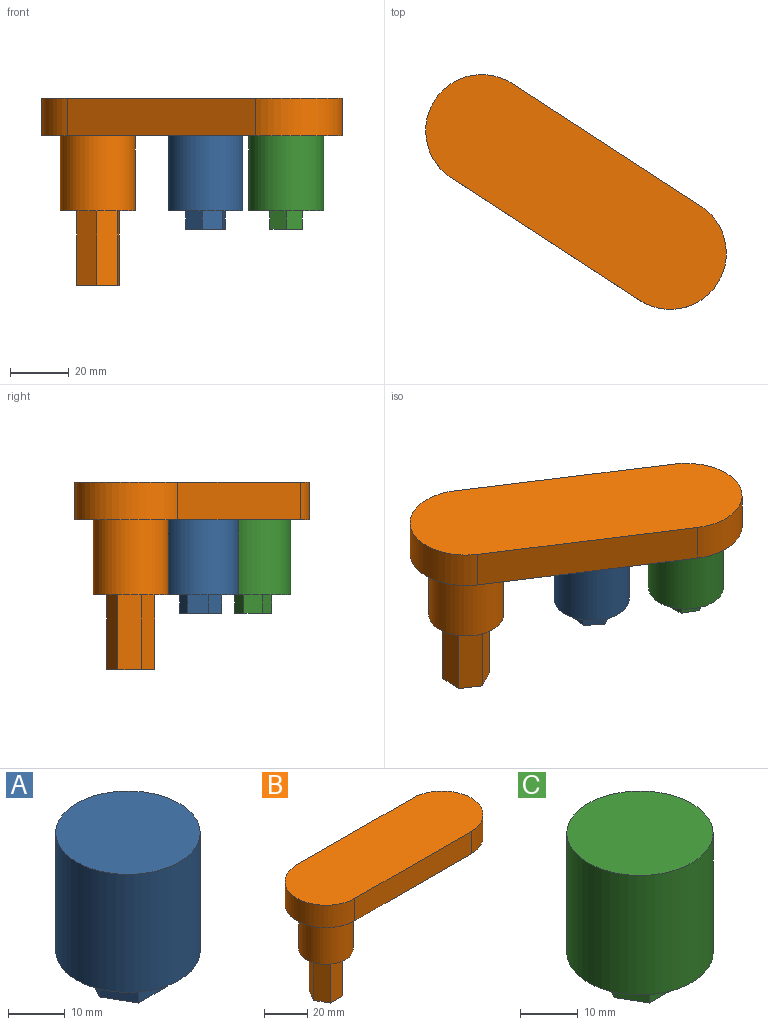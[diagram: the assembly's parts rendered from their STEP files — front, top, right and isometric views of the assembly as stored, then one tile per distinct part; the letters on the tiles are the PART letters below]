
ASSEMBLY  parts=3 mates=2
PART A: 10 faces, bbox 25.4x25.4x31.8 mm
  f0: cylinder r=12.7mm len=25.4mm, axis (0,0,1), area 2026.8mm2, adj f1,f2
  f1: plane 25.4x25.4mm, normal (0,0,-1), area 372.8mm2, adj f0,f3,f4,f5,f6,f7,f8
  f2: plane 25.4x25.4mm, normal (0,0,1), area 506.7mm2, adj f0
  f3: plane 7.18x6.35mm, normal (0,1,0), area 45.6mm2, adj f1,f4,f8,f9
  f4: plane 6.35x6.22mm, normal (0.87,0.5,0), area 45.6mm2, adj f1,f3,f5,f9
  f5: plane 6.35x6.22mm, normal (0.87,-0.5,0), area 45.6mm2, adj f1,f4,f6,f9
  f6: plane 7.18x6.35mm, normal (0,-1,0), area 45.6mm2, adj f1,f5,f7,f9
  f7: plane 6.35x6.22mm, normal (-0.87,-0.5,0), area 45.6mm2, adj f1,f6,f8,f9
  f8: plane 6.35x6.22mm, normal (-0.87,0.5,0), area 45.6mm2, adj f1,f3,f7,f9
  f9: plane 14.36x12.44mm, normal (0,0,-1), area 133.9mm2, adj f3,f4,f5,f6,f7,f8
PART B: 15 faces, bbox 114.3x38.1x63.5 mm
  f0: plane 25.4x25.4mm, normal (0,0,-1), area 335.6mm2, adj f1,f2,f3,f4,f5,f6,f7
  f1: cylinder r=12.7mm len=25.4mm, axis (0,0,-1), area 2026.8mm2, adj f0,f14
  f2: plane 25.4x8.12mm, normal (0,1,0), area 206.1mm2, adj f0,f3,f7,f8
  f3: plane 25.4x7.03mm, normal (0.87,0.5,0), area 206.1mm2, adj f0,f2,f4,f8
  f4: plane 25.4x7.03mm, normal (0.87,-0.5,0), area 206.1mm2, adj f0,f3,f5,f8
  f5: plane 25.4x8.12mm, normal (0,-1,0), area 206.1mm2, adj f0,f4,f6,f8
  f6: plane 25.4x7.03mm, normal (-0.87,-0.5,0), area 206.1mm2, adj f0,f5,f7,f8
  f7: plane 25.4x7.03mm, normal (-0.87,0.5,0), area 206.1mm2, adj f0,f2,f6,f8
  f8: plane 16.23x14.06mm, normal (0,0,-1), area 171.1mm2, adj f2,f3,f4,f5,f6,f7
  f9: plane 76.2x12.7mm, normal (0,1,0), area 967.7mm2, adj f10,f12,f13,f14
  f10: cylinder r=19.05mm len=38.1mm, axis (0,0,-1), area 760.1mm2, adj f9,f11,f13,f14
  f11: plane 76.2x12.7mm, normal (0,-1,0), area 967.7mm2, adj f10,f12,f13,f14
  f12: cylinder r=19.05mm len=38.1mm, axis (0,0,-1), area 760.1mm2, adj f9,f11,f13,f14
  f13: plane 114.3x38.1mm, normal (0,0,1), area 4043.3mm2, adj f9,f10,f11,f12
  f14: plane 114.3x38.1mm, normal (0,0,-1), area 3536.6mm2, adj f1,f9,f10,f11,f12
PART C: 10 faces, bbox 25.4x25.4x31.8 mm
  f0: cylinder r=12.7mm len=25.4mm, axis (0,0,1), area 2026.8mm2, adj f1,f2
  f1: plane 25.4x25.4mm, normal (0,0,-1), area 402mm2, adj f0,f3,f4,f5,f6,f7,f8
  f2: plane 25.4x25.4mm, normal (0,0,1), area 506.7mm2, adj f0
  f3: plane 6.35x6.35mm, normal (0,1,0), area 40.3mm2, adj f1,f4,f8,f9
  f4: plane 6.35x5.5mm, normal (0.87,0.5,0), area 40.3mm2, adj f1,f3,f5,f9
  f5: plane 6.35x5.5mm, normal (0.87,-0.5,0), area 40.3mm2, adj f1,f4,f6,f9
  f6: plane 6.35x6.35mm, normal (0,-1,0), area 40.3mm2, adj f1,f5,f7,f9
  f7: plane 6.35x5.5mm, normal (-0.87,-0.5,0), area 40.3mm2, adj f1,f6,f8,f9
  f8: plane 6.35x5.5mm, normal (-0.87,0.5,0), area 40.3mm2, adj f1,f3,f7,f9
  f9: plane 12.7x11mm, normal (0,0,-1), area 104.7mm2, adj f3,f4,f5,f6,f7,f8
PLACE A rot(axis=(0,0,-1),158.3deg) t=(71.91,-9.64,0)mm
PLACE B rot(axis=(0,0,-1),33deg) t=(0,0,0)mm
PLACE C rot(axis=(0,0,1),90deg) t=(63.88,-117.74,0)mm
MATE revolute A.f0 <-> B.f14  axis (0,0,1) through (36.52,-23.75,25.4)mm
MATE revolute C.f0 <-> B.f12  axis (0,0,1) through (63.88,-41.54,25.4)mm
